FCSTD DOCUMENT  (FreeCAD 0.16R)
Label: FrontGate
License: All rights reserved
LicenseURL: http://en.wikipedia.org/wiki/All_rights_reserved
objects: Sketcher::SketchObject×1
note: 1 computed .brp shape members not serialized (recipe doc carries the construction recipe); baked Part::Feature solids carry a one-line shape summary decoded from their .brp

FEATURE [Sketcher::SketchObject] Sketch
  sketch-geometry (8):
    g0: LineSegment StartX=2.73692 StartY=-0.690283 StartZ=0 EndX=4.23692 EndY=-0.690283 EndZ=0
    g1: LineSegment StartX=4.23692 StartY=-0.690283 StartZ=0 EndX=4.23692 EndY=-7.19028 EndZ=0
    g2: LineSegment StartX=4.23692 StartY=-7.19028 StartZ=0 EndX=2.73692 EndY=-7.19028 EndZ=0
    g3: LineSegment StartX=2.73692 StartY=-7.19028 StartZ=0 EndX=2.73692 EndY=-0.690283 EndZ=0
    g4: LineSegment StartX=-16 StartY=8 StartZ=0 EndX=0 EndY=8 EndZ=0
    g5: LineSegment StartX=0 StartY=8 StartZ=0 EndX=0 EndY=-8 EndZ=0
    g6: LineSegment StartX=0 StartY=-8 StartZ=0 EndX=-16 EndY=-8 EndZ=0
    g7: LineSegment StartX=-16 StartY=-8 StartZ=0 EndX=-16 EndY=8 EndZ=0
  constraints (22):
    c: Coincident(g0,g1)
    c: Coincident(g1,g2)
    c: Coincident(g2,g3)
    c: Coincident(g3,g0)
    c: Horizontal(g0)
    c: Horizontal(g2)
    c: Vertical(g1)
    c: Vertical(g3)
    c: Distance(g0) = 1.5
    c: Distance(g3) = 6.5
    c: Coincident(g4,g5)
    c: Coincident(g5,g6)
    c: Coincident(g6,g7)
    c: Coincident(g7,g4)
    c: Horizontal(g4)
    c: Horizontal(g6)
    c: Vertical(g5)
    c: Vertical(g7)
    c: PointOnObject(g5,g-2)
    c: Symmetric(g4,g5,g-1)
    c: Distance(g5) = 16
    c: Equal(g4,g7)
